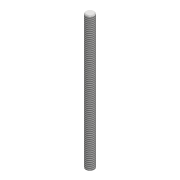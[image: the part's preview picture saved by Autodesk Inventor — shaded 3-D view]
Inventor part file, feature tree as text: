
AUTODESK INVENTOR PART (.ipt)
format: ipt  version: 2022 (Build 260153000, 153)  size: 99,840 bytes
history: native  units: mm
features: extrude x3, sketch x3, other x1, thread x1, chamfer x1
ambient origin geometry x8: Origin, YZ Plane, XZ Plane, XY Plane, X Axis, Y Axis, Z Axis, Center Point
bodies: Body1 (feature_tree)
feature tree (9):
  other  "Твердое тело1"
  extrude  "Выдавливание1"  Depth=5.0mm
  extrude  "Выдавливание2"  Depth=20.0mm
  thread  "Резьба1"
  chamfer  "Фаска1"  Distance=22.0mm
  extrude  "Выдавливание3"  Depth=485.0mm TaperAngle=0.0deg
  sketch  "Эскиз1"
  sketch  "Эскиз2"
  sketch  "Эскиз3"
